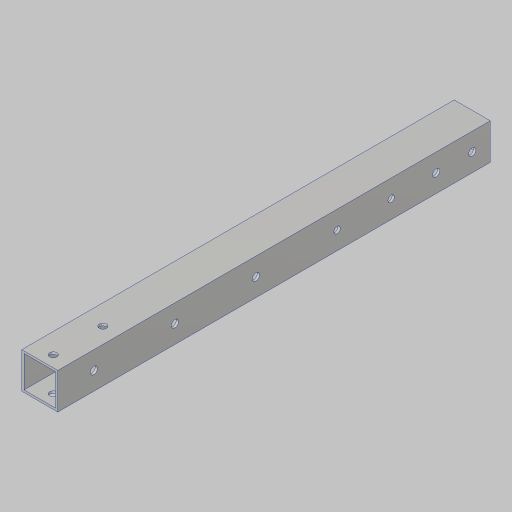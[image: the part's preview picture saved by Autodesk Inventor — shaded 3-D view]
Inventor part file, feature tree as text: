
AUTODESK INVENTOR PART (.ipt)
format: ipt  version: 2023.5 (Build 275446000, 446)  size: 145,408 bytes
history: native  units: in
note: dims shown in document units (in); Inventor stores cm internally (conversion verified against a paired STEP export)
features: hole x4, sketch x4, extrude x1, projected_geometry x1
ambient origin geometry x8: Origin, YZ Plane, XZ Plane, XY Plane, X Axis, Y Axis, Z Axis, Center Point
bodies: Solid1 (feature_tree)
feature tree (10):
  extrude  "Extrusion1"  Depth=0.5in
  hole  "Hole1"  [1 undecoded]
  hole  "Hole2"  [1 undecoded]
  hole  "Hole3"  [1 undecoded]
  hole  "Hole4"  [1 undecoded]
  sketch  "Sketch2"  dims[d4=0.0in d5=0.5in]
  sketch  "Sketch3"  dims[d6=1.0in]
  sketch  "Sketch4"  dims[d7=0.201in d8=0.75in d9=0.385in d10=0.25in d11=0.5635in d12=1.0in d13=0.8108in d14=1.375in]
  sketch  "Sketch5"  dims[d16=0.201in d17=0.75in d18=0.385in d19=0.25in d20=0.5635in d21=1.0in d22=0.8108in d23=1.0in d24=4.5in d25=0.201in d26=0.75in d27=0.375in d28=0.25in d29=0.5635in d30=1.0in d31=0.8108in d32=0.313in d33=0.0625in d34=1.5in d35=0.5in d36=2.75in d37=0.177in d38=0.75in d39=0.332in d40=0.25in d41=0.5635in d42=0.2362in d43=0.0in]
  projected_geometry  "Project Cut Edges1"
note: 4 required parameter values undecoded (feature->parameter linkage not recoverable at this tier; creation-order binding heuristic only, values carry confidence <= 0.55)
